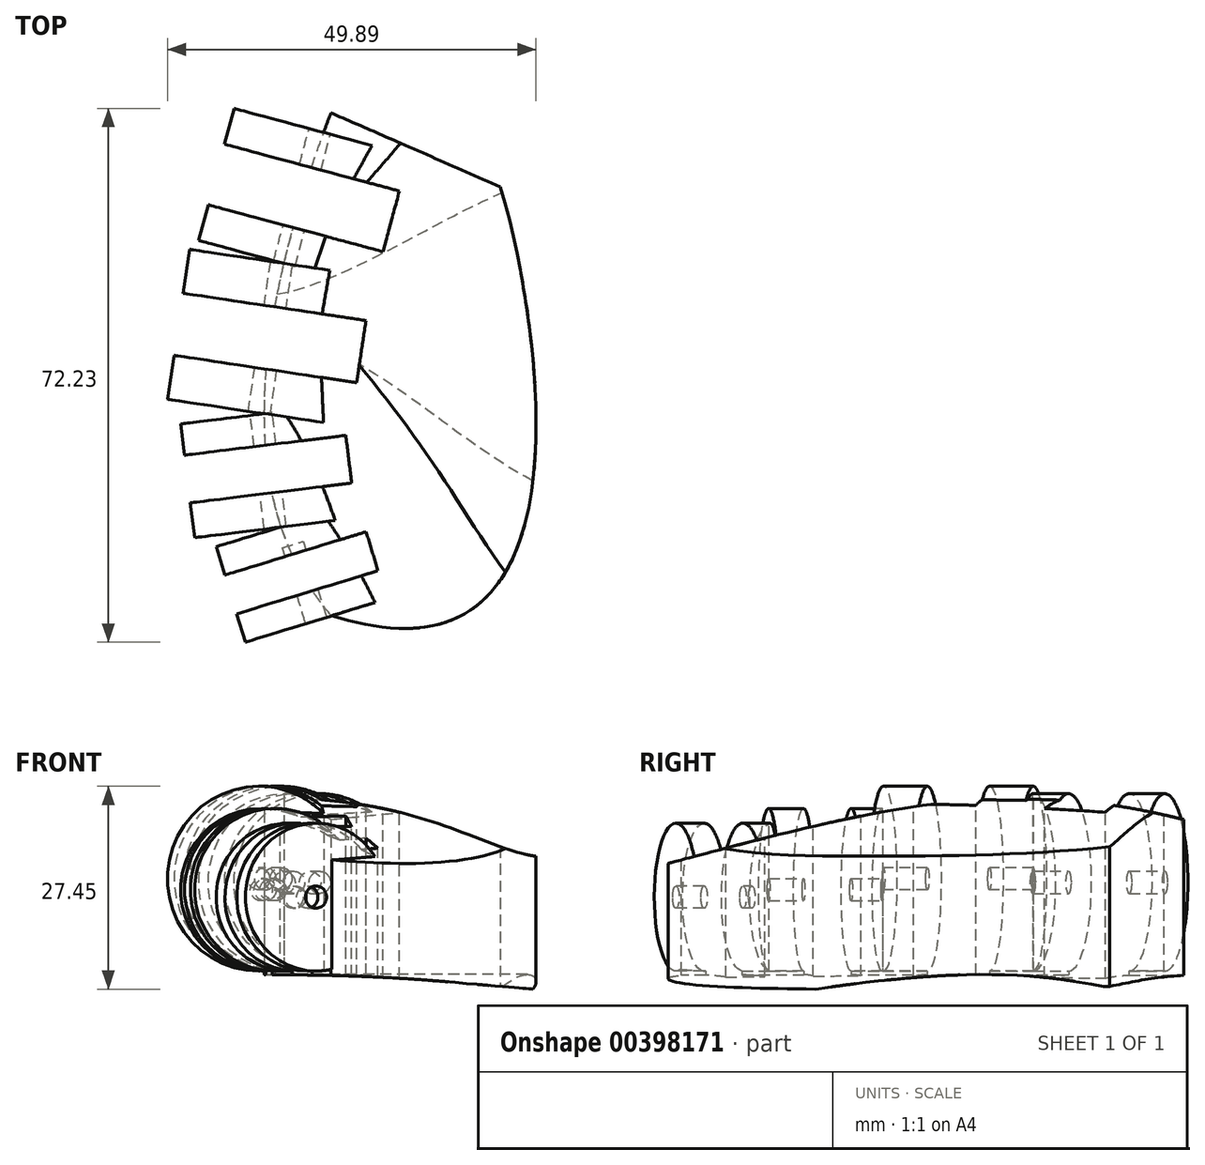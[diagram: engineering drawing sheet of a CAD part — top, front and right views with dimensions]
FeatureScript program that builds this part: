
annotation { "Feature Type Name" : "Feature", "Feature Type Description" : "" }
export const myFeature = defineFeature(function(context is Context, id is Id, definition is map)
    precondition{}
    {
        {
            var Q0;
            Q0=qCreatedBy(makeId("Top.planeOp"),FACE);
            var sketch = newSketch(context, id + "F0", { "sketchPlane" : qUnion([Q0])});
            skFitSpline(sketch, "E0", {"points": [v(0, 0) * mm, v(0, 68) * mm], "startDerivative": vector(-36, 42) * mm, "endDerivative": vector(36, 96) * mm});
            skLineSegment(sketch, "E1", {"start": v(0, 68) * mm, "end": v(22.91, 58) * mm});
            skFitSpline(sketch, "E2", {"points": [v(22.91, 58) * mm, v(0, 0) * mm], "startDerivative": vector(9, -27) * mm, "endDerivative": vector(-120, 39) * mm});
            skSolve(sketch);
        }
        {
            var Q0;
            Q0 = qSketchRegion(id + "F0", true);
            extrude(context, id + "F1", {"entities" : qUnion([Q0]), "depth" : 30 * mm});
        }
        {
            var Q0;
            Q0=qCreatedBy(makeId("Right.planeOp"),FACE);
            var sketch = newSketch(context, id + "F2", { "sketchPlane" : qUnion([Q0])});
            skFitSpline(sketch, "E3", {"points": [v(68, 26) * mm, v(-2, 20) * mm], "startDerivative": vector(-72, 18) * mm, "endDerivative": vector(-90, -24) * mm});
            skFitSpline(sketch, "E4", {"points": [v(68, 1) * mm, v(0, 0) * mm], "startDerivative": vector(-54, 12) * mm, "endDerivative": vector(-129, -24) * mm});
            skLineSegment(sketch, "E5", {"start": v(68, 26) * mm, "end": v(68, 1) * mm});
            skLineSegment(sketch, "E6", {"start": v(0, 0) * mm, "end": v(-2, 0) * mm});
            skLineSegment(sketch, "E7", {"start": v(-2, 0) * mm, "end": v(-2, 20) * mm});
            skLineSegment(sketch, "E8.bottom", {"start": v(70, 33) * mm, "end": v(-4, 33) * mm});
            skLineSegment(sketch, "E8.top", {"start": v(70, -4) * mm, "end": v(-4, -4) * mm});
            skLineSegment(sketch, "E8.left", {"start": v(70, 33) * mm, "end": v(70, -4) * mm});
            skLineSegment(sketch, "E8.right", {"start": v(-4, 33) * mm, "end": v(-4, -4) * mm});
            skSolve(sketch);
        }
        {
            var Q0;
            Q0 = qSketchRegion(id + "F2", true);
            extrude(context, id + "F3", {"entities" : qUnion([Q0]), "operationType" : NewBodyOperationType.REMOVE, "endBound" : BoundingType.SYMMETRIC, "oppositeDirection" : true, "depth" : 81.4 * mm});
        }
        {
            var Q0;
            Q0=qCreatedBy(makeId("Front.planeOp"),FACE);
            var sketch = newSketch(context, id + "F4", { "sketchPlane" : qUnion([Q0])});
            skFitSpline(sketch, "E9", {"points": [v(-9, 29) * mm, v(28, 21) * mm], "startDerivative": vector(66, 0) * mm, "endDerivative": vector(24, -3) * mm});
            skLineSegment(sketch, "E10", {"start": v(28, 21) * mm, "end": v(28, 3) * mm});
            skFitSpline(sketch, "E11", {"points": [v(28, 3) * mm, v(-9, 5) * mm], "startDerivative": vector(-39, 3) * mm, "endDerivative": vector(-54.88, 0) * mm});
            skLineSegment(sketch, "E12", {"start": v(-9, 5) * mm, "end": v(-9, 29) * mm});
            skSolve(sketch);
        }
        {
            var Q0;
            Q0 = qSketchRegion(id + "F4", true);
            extrude(context, id + "F5", {"entities" : qUnion([Q0]), "operationType" : NewBodyOperationType.INTERSECT, "endBound" : BoundingType.SYMMETRIC, "oppositeDirection" : true, "depth" : 150.8 * mm});
        }
        {
            var Q0;
            Q0=qCreatedBy(makeId("Top.planeOp"),FACE);
            var sketch = newSketch(context, id + "F6", { "sketchPlane" : qUnion([Q0])});
            skLineSegment(sketch, "E13", {"start": v(0, 0) * mm, "end": v(72.45, 0) * mm, "construction": true});
            skLineSegment(sketch, "E14", {"start": v(-3.91, 56.54) * mm, "end": v(37.87, 45.35) * mm, "construction": true});
            skLineSegment(sketch, "E15", {"start": v(-4, 5.74) * mm, "end": v(26.43, 15.05) * mm, "construction": true});
            skLineSegment(sketch, "E16", {"start": v(-8.25, 37.53) * mm, "end": v(30.6, 31.73) * mm, "construction": true});
            skLineSegment(sketch, "E17", {"start": v(-8.48, 19.53) * mm, "end": v(33.43, 24.68) * mm, "construction": true});
            skSolve(sketch);
        }
        {
            var Q0;
            Q0=sQuery(id+"F6.wireOp",VERTEX,"E14.start");
            var Q1;
            Q1=sQuery(id+"F6.wireOp",EDGE,"E14");
            cPlane(context, id + "F7", {"entities" : qUnion([Q0, Q1]), "cplaneType" : CPlaneType.LINE_POINT, "offset" : 25 * mm, "width" : 150 * mm, "height" : 150 * mm});
        }
        {
            var Q0;
            Q0=sQuery(id+"F6.wireOp",VERTEX,"E16.start");
            var Q1;
            Q1=sQuery(id+"F6.wireOp",EDGE,"E16");
            cPlane(context, id + "F8", {"entities" : qUnion([Q0, Q1]), "cplaneType" : CPlaneType.LINE_POINT, "offset" : 25 * mm, "width" : 150 * mm, "height" : 150 * mm});
        }
        {
            var Q0;
            Q0=sQuery(id+"F6.wireOp",VERTEX,"E17.start");
            var Q1;
            Q1=sQuery(id+"F6.wireOp",EDGE,"E17");
            cPlane(context, id + "F9", {"entities" : qUnion([Q0, Q1]), "cplaneType" : CPlaneType.LINE_POINT, "offset" : 25 * mm, "width" : 150 * mm, "height" : 150 * mm});
        }
        {
            var Q0;
            Q0=sQuery(id+"F6.wireOp",VERTEX,"E15.start");
            var Q1;
            Q1=sQuery(id+"F6.wireOp",EDGE,"E15");
            cPlane(context, id + "F10", {"entities" : qUnion([Q0, Q1]), "cplaneType" : CPlaneType.LINE_POINT, "offset" : 25 * mm, "width" : 150 * mm, "height" : 150 * mm});
        }
        {
            var Q0;
            Q0=sQuery(id+"F6.wireOp",EDGE,"E14");
            cPlane(context, id + "F11", {"entities" : qUnion([Q0]), "cplaneType" : CPlaneType.LINE_ANGLE, "offset" : 25 * mm, "angle" : 0 * degree, "width" : 150 * mm, "height" : 150 * mm});
        }
        {
            var Q0;
            Q0=sQuery(id+"F6.wireOp",EDGE,"E16");
            cPlane(context, id + "F12", {"entities" : qUnion([Q0]), "cplaneType" : CPlaneType.LINE_ANGLE, "offset" : 25 * mm, "angle" : 0 * degree, "width" : 150 * mm, "height" : 150 * mm});
        }
        {
            var Q0;
            Q0=sQuery(id+"F6.wireOp",EDGE,"E17");
            cPlane(context, id + "F13", {"entities" : qUnion([Q0]), "cplaneType" : CPlaneType.LINE_ANGLE, "offset" : 25 * mm, "angle" : 0 * degree, "width" : 150 * mm, "height" : 150 * mm});
        }
        {
            var Q0;
            Q0=sQuery(id+"F6.wireOp",EDGE,"E15");
            cPlane(context, id + "F14", {"entities" : qUnion([Q0]), "cplaneType" : CPlaneType.LINE_ANGLE, "offset" : 25 * mm, "angle" : 0 * degree, "width" : 150 * mm, "height" : 150 * mm});
        }
        {
            var Q0;
            Q0=qCreatedBy(id+"F11.planeOp",FACE);
            var sketch = newSketch(context, id + "F15", { "sketchPlane" : qUnion([Q0])});
            skCircle(sketch, "E18", {"center": v(18.41, 17.5) * mm, "radius": 12 * mm});
            skSolve(sketch);
        }
        {
            var Q0;
            Q0 = qSketchRegion(id + "F15", true);
            extrude(context, id + "F16", {"entities" : qUnion([Q0]), "operationType" : NewBodyOperationType.ADD, "endBound" : BoundingType.SYMMETRIC, "depth" : 18.5 * mm});
        }
        {
            var Q0;
            Q0=qCreatedBy(id+"F7.planeOp",FACE);
            var sketch = newSketch(context, id + "F17", { "sketchPlane" : qUnion([Q0])});
            skLineSegment(sketch, "E19.bottom", {"start": v(57.86, 4) * mm, "end": v(49.36, 4) * mm});
            skLineSegment(sketch, "E19.top", {"start": v(57.86, 34) * mm, "end": v(49.36, 34) * mm});
            skLineSegment(sketch, "E19.left", {"start": v(57.86, 4) * mm, "end": v(57.86, 34) * mm});
            skLineSegment(sketch, "E19.right", {"start": v(49.36, 4) * mm, "end": v(49.36, 34) * mm});
            skSolve(sketch);
        }
        {
            var Q0;
            Q0 = qSketchRegion(id + "F17", true);
            extrude(context, id + "F18", {"entities" : qUnion([Q0]), "operationType" : NewBodyOperationType.REMOVE, "endBound" : BoundingType.SYMMETRIC, "oppositeDirection" : true, "depth" : 25 * mm});
        }
        {
            var Q0;
            Q0=qCreatedBy(id+"F12.planeOp",FACE);
            var sketch = newSketch(context, id + "F19", { "sketchPlane" : qUnion([Q0])});
            skCircle(sketch, "E20", {"center": v(13.71, 18) * mm, "radius": 12.5 * mm});
            skSolve(sketch);
        }
        {
            var Q0;
            Q0 = qSketchRegion(id + "F19", true);
            extrude(context, id + "F20", {"entities" : qUnion([Q0]), "operationType" : NewBodyOperationType.ADD, "endBound" : BoundingType.SYMMETRIC, "depth" : 20.5 * mm});
        }
        {
            var Q0;
            Q0=qCreatedBy(id+"F8.planeOp",FACE);
            var sketch = newSketch(context, id + "F21", { "sketchPlane" : qUnion([Q0])});
            skLineSegment(sketch, "E21.bottom", {"start": v(40.15, 4) * mm, "end": v(31.65, 4) * mm});
            skLineSegment(sketch, "E21.top", {"start": v(40.15, 31) * mm, "end": v(31.65, 31) * mm});
            skLineSegment(sketch, "E21.left", {"start": v(40.15, 4) * mm, "end": v(40.15, 31) * mm});
            skLineSegment(sketch, "E21.right", {"start": v(31.65, 4) * mm, "end": v(31.65, 31) * mm});
            skSolve(sketch);
        }
        {
            var Q0;
            Q0 = qSketchRegion(id + "F21", true);
            extrude(context, id + "F22", {"entities" : qUnion([Q0]), "operationType" : NewBodyOperationType.REMOVE, "endBound" : BoundingType.SYMMETRIC, "depth" : 25 * mm});
        }
        {
            var Q0;
            Q0=qCreatedBy(id+"F13.planeOp",FACE);
            var sketch = newSketch(context, id + "F23", { "sketchPlane" : qUnion([Q0])});
            skCircle(sketch, "E22", {"center": v(6.04, 16.5) * mm, "radius": 11 * mm});
            skSolve(sketch);
        }
        {
            var Q0;
            Q0 = qSketchRegion(id + "F23", true);
            extrude(context, id + "F24", {"entities" : qUnion([Q0]), "operationType" : NewBodyOperationType.ADD, "endBound" : BoundingType.SYMMETRIC, "depth" : 15.5 * mm});
        }
        {
            var Q0;
            Q0=qCreatedBy(id+"F9.planeOp",FACE);
            var sketch = newSketch(context, id + "F25", { "sketchPlane" : qUnion([Q0])});
            skLineSegment(sketch, "E23.bottom", {"start": v(23.92, 4.5) * mm, "end": v(17.42, 4.5) * mm});
            skLineSegment(sketch, "E23.top", {"start": v(23.92, 28.5) * mm, "end": v(17.42, 28.5) * mm});
            skLineSegment(sketch, "E23.left", {"start": v(23.92, 4.5) * mm, "end": v(23.92, 28.5) * mm});
            skLineSegment(sketch, "E23.right", {"start": v(17.42, 4.5) * mm, "end": v(17.42, 28.5) * mm});
            skSolve(sketch);
        }
        {
            var Q0;
            Q0 = qSketchRegion(id + "F25", true);
            extrude(context, id + "F26", {"entities" : qUnion([Q0]), "operationType" : NewBodyOperationType.REMOVE, "endBound" : BoundingType.SYMMETRIC, "oppositeDirection" : true, "depth" : 22 * mm});
        }
        {
            var Q0;
            Q0=qCreatedBy(id+"F14.planeOp",FACE);
            var sketch = newSketch(context, id + "F27", { "sketchPlane" : qUnion([Q0])});
            skCircle(sketch, "E24", {"center": v(2.15, 15.5) * mm, "radius": 10 * mm});
            skSolve(sketch);
        }
        {
            var Q0;
            Q0 = qSketchRegion(id + "F27", true);
            extrude(context, id + "F28", {"entities" : qUnion([Q0]), "operationType" : NewBodyOperationType.ADD, "endBound" : BoundingType.SYMMETRIC, "depth" : 13.5 * mm});
        }
        {
            var Q0;
            Q0=qCreatedBy(id+"F10.planeOp",FACE);
            var sketch = newSketch(context, id + "F29", { "sketchPlane" : qUnion([Q0])});
            skLineSegment(sketch, "E25.bottom", {"start": v(9.41, 4) * mm, "end": v(3.91, 4) * mm});
            skLineSegment(sketch, "E25.top", {"start": v(9.41, 28) * mm, "end": v(3.91, 28) * mm});
            skLineSegment(sketch, "E25.left", {"start": v(9.41, 4) * mm, "end": v(9.41, 28) * mm});
            skLineSegment(sketch, "E25.right", {"start": v(3.91, 4) * mm, "end": v(3.91, 28) * mm});
            skSolve(sketch);
        }
        {
            var Q0;
            Q0 = qSketchRegion(id + "F29", true);
            extrude(context, id + "F30", {"entities" : qUnion([Q0]), "operationType" : NewBodyOperationType.REMOVE, "endBound" : BoundingType.SYMMETRIC, "oppositeDirection" : true, "depth" : 20 * mm});
        }
        {
            var Q0;
            Q0=qCreatedBy(id+"F11.planeOp",FACE);
            var sketch = newSketch(context, id + "F31", { "sketchPlane" : qUnion([Q0])});
            skCircle(sketch, "E26", {"center": v(18.41, 17.5) * mm, "radius": 1.5 * mm});
            skSolve(sketch);
        }
        {
            var Q0;
            Q0 = qSketchRegion(id + "F31", true);
            extrude(context, id + "F32", {"entities" : qUnion([Q0]), "operationType" : NewBodyOperationType.REMOVE, "endBound" : BoundingType.SYMMETRIC, "oppositeDirection" : true, "depth" : 18.5 * mm});
        }
        {
            var Q0;
            Q0=qCreatedBy(id+"F12.planeOp",FACE);
            var sketch = newSketch(context, id + "F33", { "sketchPlane" : qUnion([Q0])});
            skCircle(sketch, "E27", {"center": v(13.71, 18) * mm, "radius": 1.5 * mm});
            skSolve(sketch);
        }
        {
            var Q0;
            Q0 = qSketchRegion(id + "F33", true);
            extrude(context, id + "F34", {"entities" : qUnion([Q0]), "operationType" : NewBodyOperationType.REMOVE, "endBound" : BoundingType.SYMMETRIC, "depth" : 20.5 * mm});
        }
        {
            var Q0;
            Q0=qCreatedBy(id+"F13.planeOp",FACE);
            var sketch = newSketch(context, id + "F35", { "sketchPlane" : qUnion([Q0])});
            skCircle(sketch, "E28", {"center": v(6.04, 16.5) * mm, "radius": 1.5 * mm});
            skSolve(sketch);
        }
        {
            var Q0;
            Q0 = qSketchRegion(id + "F35", true);
            extrude(context, id + "F36", {"entities" : qUnion([Q0]), "operationType" : NewBodyOperationType.REMOVE, "endBound" : BoundingType.SYMMETRIC, "oppositeDirection" : true, "depth" : 15.5 * mm});
        }
        {
            var Q0;
            Q0=makeQuery(id+"F30.boolean.opBoolean","COPY",FACE,{"derivedFrom":makeQuery(id+"F30.opExtrude","SWEPT_FACE",FACE,{"disambiguationData":[OSD([sQuery(id+"F29.wireOp",EDGE,"E25.right")])]})});
            var sketch = newSketch(context, id + "F37", { "sketchPlane" : qUnion([Q0])});
            skCircle(sketch, "E29", {"center": v(2.15, 15.5) * mm, "radius": 1.5 * mm});
            skSolve(sketch);
        }
        {
            var Q0;
            Q0 = qSketchRegion(id + "F37", true);
            extrude(context, id + "F38", {"entities" : qUnion([Q0]), "operationType" : NewBodyOperationType.REMOVE, "endBound" : BoundingType.SYMMETRIC, "depth" : 13.5 * mm});
        }
    });
